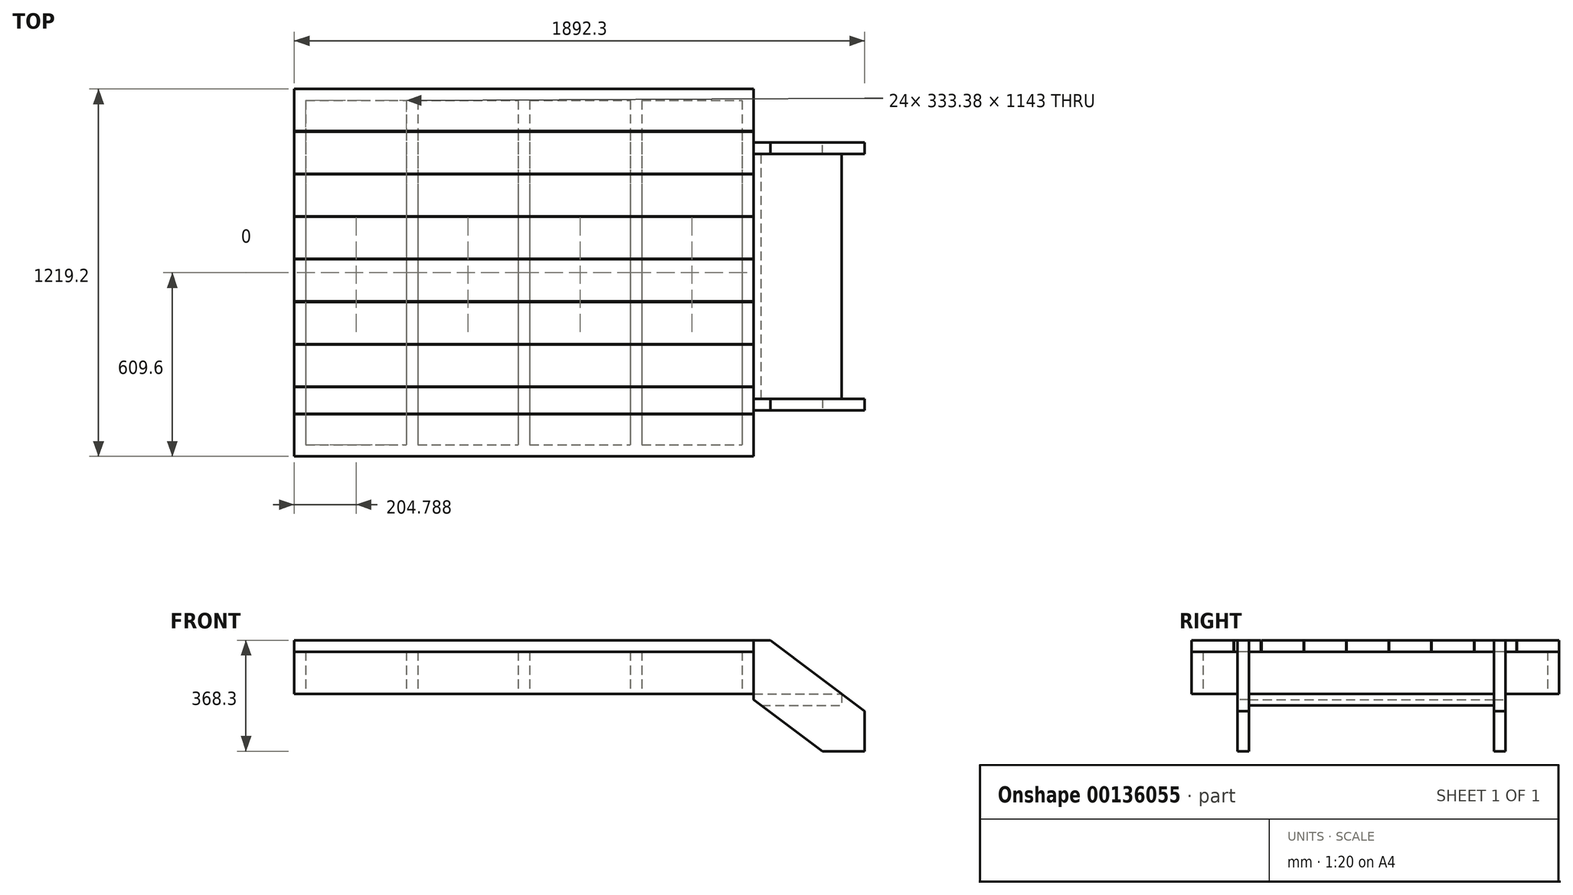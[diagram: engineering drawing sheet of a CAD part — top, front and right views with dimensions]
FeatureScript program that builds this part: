
annotation { "Feature Type Name" : "Feature", "Feature Type Description" : "" }
export const myFeature = defineFeature(function(context is Context, id is Id, definition is map)
    precondition{}
    {
        {
            var Q0;
            Q0=qCreatedBy(makeId("Top.planeOp"),FACE);
            var sketch = newSketch(context, id + "F0", { "sketchPlane" : qUnion([Q0])});
            skLineSegment(sketch, "E0.bottom", {"start": v(-762, 609.6) * mm, "end": v(762, 609.6) * mm});
            skLineSegment(sketch, "E0.top", {"start": v(-762, -609.6) * mm, "end": v(762, -609.6) * mm});
            skLineSegment(sketch, "E0.left", {"start": v(-762, 609.6) * mm, "end": v(-762, -609.6) * mm});
            skLineSegment(sketch, "E0.right", {"start": v(762, 609.6) * mm, "end": v(762, -609.6) * mm});
            skLineSegment(sketch, "E1.bottom", {"start": v(-723.9, 571.5) * mm, "end": v(-390.52, 571.5) * mm});
            skLineSegment(sketch, "E1.top", {"start": v(-723.9, -571.5) * mm, "end": v(-390.53, -571.5) * mm});
            skLineSegment(sketch, "E1.left", {"start": v(-723.9, 571.5) * mm, "end": v(-723.9, -571.5) * mm});
            skLineSegment(sketch, "E1.right", {"start": v(-390.52, 571.5) * mm, "end": v(-390.53, -571.5) * mm});
            skLineSegment(sketch, "E2.bottom", {"start": v(-352.42, 571.5) * mm, "end": v(-19.05, 571.5) * mm});
            skLineSegment(sketch, "E2.top", {"start": v(-352.43, -571.5) * mm, "end": v(-19.05, -571.5) * mm});
            skLineSegment(sketch, "E2.left", {"start": v(-352.42, 571.5) * mm, "end": v(-352.43, -571.5) * mm});
            skLineSegment(sketch, "E2.right", {"start": v(-19.05, 571.5) * mm, "end": v(-19.05, -571.5) * mm});
            skLineSegment(sketch, "E3.bottom", {"start": v(19.05, 571.5) * mm, "end": v(352.43, 571.5) * mm});
            skLineSegment(sketch, "E3.top", {"start": v(19.05, -571.5) * mm, "end": v(352.43, -571.5) * mm});
            skLineSegment(sketch, "E3.left", {"start": v(19.05, 571.5) * mm, "end": v(19.05, -571.5) * mm});
            skLineSegment(sketch, "E3.right", {"start": v(352.43, 571.5) * mm, "end": v(352.43, -571.5) * mm});
            skLineSegment(sketch, "E4", {"start": v(0, 0) * mm, "end": v(0, -270.05) * mm, "construction": true});
            skLineSegment(sketch, "E5", {"start": v(-150.6, 0) * mm, "end": v(0, 0) * mm, "construction": true});
            skLineSegment(sketch, "E6.bottom", {"start": v(390.53, 571.5) * mm, "end": v(723.9, 571.5) * mm});
            skLineSegment(sketch, "E6.top", {"start": v(390.52, -571.5) * mm, "end": v(723.9, -571.5) * mm});
            skLineSegment(sketch, "E6.left", {"start": v(390.53, 571.5) * mm, "end": v(390.52, -571.5) * mm});
            skLineSegment(sketch, "E6.right", {"start": v(723.9, 571.5) * mm, "end": v(723.9, -571.5) * mm});
            skSolve(sketch);
        }
        {
            var Q0;
            Q0=makeQuery(id+"F0.imprint","IMPRINT",FACE,{"disambiguationData":[TD([[makeQuery(id+"F0.imprint","IMPRINT",EDGE,{"derivedFrom":sQuery(id+"F0.wireOp",EDGE,"E0.bottom")}),-1.0]])]});
            extrude(context, id + "F1", {"entities" : qUnion([Q0]), "depth" : 139.7 * mm});
        }
        {
            var Q0;
            Q0=makeQuery(id+"F1.opExtrude","SWEPT_FACE",FACE,{"disambiguationData":[OSD([sQuery(id+"F0.wireOp",EDGE,"E0.left")])]});
            var sketch = newSketch(context, id + "F2", { "sketchPlane" : qUnion([Q0])});
            skLineSegment(sketch, "E7.bottom", {"start": v(-609.6, 177.8) * mm, "end": v(-469.9, 177.8) * mm});
            skLineSegment(sketch, "E7.top", {"start": v(-609.6, 139.7) * mm, "end": v(-469.9, 139.7) * mm});
            skLineSegment(sketch, "E7.left", {"start": v(-609.6, 177.8) * mm, "end": v(-609.6, 139.7) * mm});
            skLineSegment(sketch, "E7.right", {"start": v(-469.9, 177.8) * mm, "end": v(-469.9, 139.7) * mm});
            skLineSegment(sketch, "E8.bottom", {"start": v(-468.31, 177.8) * mm, "end": v(-328.61, 177.8) * mm});
            skLineSegment(sketch, "E8.top", {"start": v(-468.31, 139.7) * mm, "end": v(-328.61, 139.7) * mm});
            skLineSegment(sketch, "E8.left", {"start": v(-468.31, 177.8) * mm, "end": v(-468.31, 139.7) * mm});
            skLineSegment(sketch, "E8.right", {"start": v(-328.61, 177.8) * mm, "end": v(-328.61, 139.7) * mm});
            skLineSegment(sketch, "E9.bottom", {"start": v(-327.02, 177.8) * mm, "end": v(-187.32, 177.8) * mm});
            skLineSegment(sketch, "E9.top", {"start": v(-327.02, 139.7) * mm, "end": v(-187.32, 139.7) * mm});
            skLineSegment(sketch, "E9.left", {"start": v(-327.02, 177.8) * mm, "end": v(-327.02, 139.7) * mm});
            skLineSegment(sketch, "E9.right", {"start": v(-187.32, 177.8) * mm, "end": v(-187.32, 139.7) * mm});
            skLineSegment(sketch, "E10.bottom", {"start": v(-185.74, 177.8) * mm, "end": v(-46.04, 177.8) * mm});
            skLineSegment(sketch, "E10.top", {"start": v(-185.74, 139.7) * mm, "end": v(-46.04, 139.7) * mm});
            skLineSegment(sketch, "E10.left", {"start": v(-185.74, 177.8) * mm, "end": v(-185.74, 139.7) * mm});
            skLineSegment(sketch, "E10.right", {"start": v(-46.04, 177.8) * mm, "end": v(-46.04, 139.7) * mm});
            skLineSegment(sketch, "E11.bottom", {"start": v(-44.45, 177.8) * mm, "end": v(95.25, 177.8) * mm});
            skLineSegment(sketch, "E11.top", {"start": v(-44.45, 139.7) * mm, "end": v(95.25, 139.7) * mm});
            skLineSegment(sketch, "E11.left", {"start": v(-44.45, 177.8) * mm, "end": v(-44.45, 139.7) * mm});
            skLineSegment(sketch, "E11.right", {"start": v(95.25, 177.8) * mm, "end": v(95.25, 139.7) * mm});
            skLineSegment(sketch, "E12.bottom", {"start": v(96.84, 177.8) * mm, "end": v(236.54, 177.8) * mm});
            skLineSegment(sketch, "E12.top", {"start": v(96.84, 139.7) * mm, "end": v(236.54, 139.7) * mm});
            skLineSegment(sketch, "E12.left", {"start": v(96.84, 177.8) * mm, "end": v(96.84, 139.7) * mm});
            skLineSegment(sketch, "E12.right", {"start": v(236.54, 177.8) * mm, "end": v(236.54, 139.7) * mm});
            skLineSegment(sketch, "E13.bottom", {"start": v(238.13, 177.8) * mm, "end": v(377.83, 177.8) * mm});
            skLineSegment(sketch, "E13.top", {"start": v(238.13, 139.7) * mm, "end": v(377.83, 139.7) * mm});
            skLineSegment(sketch, "E13.left", {"start": v(238.13, 177.8) * mm, "end": v(238.13, 139.7) * mm});
            skLineSegment(sketch, "E13.right", {"start": v(377.83, 177.8) * mm, "end": v(377.83, 139.7) * mm});
            skLineSegment(sketch, "E14.bottom", {"start": v(379.41, 177.8) * mm, "end": v(468.31, 177.8) * mm});
            skLineSegment(sketch, "E14.top", {"start": v(379.41, 139.7) * mm, "end": v(468.31, 139.7) * mm});
            skLineSegment(sketch, "E14.left", {"start": v(379.41, 177.8) * mm, "end": v(379.41, 139.7) * mm});
            skLineSegment(sketch, "E14.right", {"start": v(468.31, 177.8) * mm, "end": v(468.31, 139.7) * mm});
            skLineSegment(sketch, "E15.bottom", {"start": v(469.9, 177.8) * mm, "end": v(609.6, 177.8) * mm});
            skLineSegment(sketch, "E15.top", {"start": v(469.9, 139.7) * mm, "end": v(609.6, 139.7) * mm});
            skLineSegment(sketch, "E15.left", {"start": v(469.9, 177.8) * mm, "end": v(469.9, 139.7) * mm});
            skLineSegment(sketch, "E15.right", {"start": v(609.6, 177.8) * mm, "end": v(609.6, 139.7) * mm});
            skSolve(sketch);
        }
        {
            var Q0;
            Q0=makeQuery(id+"F2.imprint","IMPRINT",FACE,{"disambiguationData":[TD([[makeQuery(id+"F2.imprint","IMPRINT",EDGE,{"derivedFrom":sQuery(id+"F2.wireOp",EDGE,"E10.bottom")}),-1.0]])]});
            var Q1;
            Q1=makeQuery(id+"F2.imprint","IMPRINT",FACE,{"disambiguationData":[TD([[makeQuery(id+"F2.imprint","IMPRINT",EDGE,{"derivedFrom":sQuery(id+"F2.wireOp",EDGE,"E11.bottom")}),-1.0]])]});
            var Q2;
            Q2=makeQuery(id+"F2.imprint","IMPRINT",FACE,{"disambiguationData":[TD([[makeQuery(id+"F2.imprint","IMPRINT",EDGE,{"derivedFrom":sQuery(id+"F2.wireOp",EDGE,"E14.bottom")}),-1.0]])]});
            var Q3;
            Q3=makeQuery(id+"F2.imprint","IMPRINT",FACE,{"disambiguationData":[TD([[makeQuery(id+"F2.imprint","IMPRINT",EDGE,{"derivedFrom":sQuery(id+"F2.wireOp",EDGE,"E15.bottom")}),-1.0]])]});
            var Q4;
            Q4=makeQuery(id+"F2.imprint","IMPRINT",FACE,{"disambiguationData":[TD([[makeQuery(id+"F2.imprint","IMPRINT",EDGE,{"derivedFrom":sQuery(id+"F2.wireOp",EDGE,"E12.bottom")}),-1.0]])]});
            var Q5;
            Q5=makeQuery(id+"F2.imprint","IMPRINT",FACE,{"disambiguationData":[TD([[makeQuery(id+"F2.imprint","IMPRINT",EDGE,{"derivedFrom":sQuery(id+"F2.wireOp",EDGE,"E13.bottom")}),-1.0]])]});
            var Q6;
            Q6=makeQuery(id+"F2.imprint","IMPRINT",FACE,{"disambiguationData":[TD([[makeQuery(id+"F2.imprint","IMPRINT",EDGE,{"derivedFrom":sQuery(id+"F2.wireOp",EDGE,"E7.bottom")}),-1.0]])]});
            var Q7;
            Q7=makeQuery(id+"F2.imprint","IMPRINT",FACE,{"disambiguationData":[TD([[makeQuery(id+"F2.imprint","IMPRINT",EDGE,{"derivedFrom":sQuery(id+"F2.wireOp",EDGE,"E8.bottom")}),-1.0]])]});
            var Q8;
            Q8=makeQuery(id+"F2.imprint","IMPRINT",FACE,{"disambiguationData":[TD([[makeQuery(id+"F2.imprint","IMPRINT",EDGE,{"derivedFrom":sQuery(id+"F2.wireOp",EDGE,"E9.bottom")}),-1.0]])]});
            var Q9;
            Q9=makeQuery(id+"F1.opExtrude","SWEPT_FACE",FACE,{"disambiguationData":[OSD([sQuery(id+"F0.wireOp",EDGE,"E0.right")])]});
            extrude(context, id + "F3", {"entities" : qUnion([Q0, Q1, Q2, Q3, Q4, Q5, Q6, Q7, Q8]), "endBound" : BoundingType.UP_TO_SURFACE, "oppositeDirection" : true, "endBoundEntityFace" : qUnion([Q9]), "depth" : 1524 * mm});
        }
        {
            var Q0;
            Q0=makeQuery(id+"F1.opExtrude","SWEPT_FACE",FACE,{"disambiguationData":[OSD([sQuery(id+"F0.wireOp",EDGE,"E0.top")])]});
            cPlane(context, id + "F4", {"entities" : qUnion([Q0]), "cplaneType" : CPlaneType.OFFSET, "offset" : 152.4 * mm, "oppositeDirection" : true, "width" : 152.4 * mm, "height" : 152.4 * mm});
        }
        {
            var Q0;
            Q0=qCreatedBy(id+"F4.planeOp",FACE);
            var sketch = newSketch(context, id + "F5", { "sketchPlane" : qUnion([Q0])});
            skLineSegment(sketch, "E16", {"start": v(762, 177.8) * mm, "end": v(762, -19.05) * mm});
            skLineSegment(sketch, "E17", {"start": v(762, -19.05) * mm, "end": v(990.6, -190.5) * mm});
            skLineSegment(sketch, "E18", {"start": v(990.6, -190.5) * mm, "end": v(1130.3, -190.5) * mm});
            skLineSegment(sketch, "E19", {"start": v(1130.3, -190.5) * mm, "end": v(1130.3, -57.15) * mm});
            skLineSegment(sketch, "E20", {"start": v(1130.3, -57.15) * mm, "end": v(817.03, 177.8) * mm});
            skLineSegment(sketch, "E21", {"start": v(817.03, 177.8) * mm, "end": v(762, 177.8) * mm});
            skLineSegment(sketch, "E22", {"start": v(762, 0) * mm, "end": v(1054.1, 0) * mm, "construction": true});
            skSolve(sketch);
        }
        {
            var Q0;
            Q0=makeQuery(id+"F5.imprint","IMPRINT",FACE,{"disambiguationData":[TD([[makeQuery(id+"F5.imprint","IMPRINT",EDGE,{"derivedFrom":sQuery(id+"F5.wireOp",EDGE,"E16")}),1.0]])]});
            extrude(context, id + "F6", {"entities" : qUnion([Q0]), "oppositeDirection" : true, "depth" : 38.1 * mm});
        }
        {
            var Q0;
            Q0=makeQuery(id+"F6.opExtrude","CAP_FACE",FACE,{"disambiguationData":[OSD([sQuery(id+"F5.wireOp",EDGE,"E16"),sQuery(id+"F5.wireOp",EDGE,"E17"),sQuery(id+"F5.wireOp",EDGE,"E18"),sQuery(id+"F5.wireOp",EDGE,"E19"),sQuery(id+"F5.wireOp",EDGE,"E20"),sQuery(id+"F5.wireOp",EDGE,"E21")])],"isStart":false});
            cPlane(context, id + "F7", {"entities" : qUnion([Q0]), "cplaneType" : CPlaneType.OFFSET, "offset" : 406.4 * mm, "width" : 152.4 * mm, "height" : 152.4 * mm});
        }
        {
            var Q0;
            Q0=makeQuery(id+"F6.opExtrude","SWEPT_BODY",BODY,{"disambiguationData":[OSD([sQuery(id+"F5.wireOp",EDGE,"E16"),sQuery(id+"F5.wireOp",EDGE,"E17"),sQuery(id+"F5.wireOp",EDGE,"E18"),sQuery(id+"F5.wireOp",EDGE,"E19"),sQuery(id+"F5.wireOp",EDGE,"E20"),sQuery(id+"F5.wireOp",EDGE,"E21")])]});
            var Q1;
            Q1=qCreatedBy(id+"F7.planeOp",FACE);
            mirror(context, id + "F8", {"entities" : qUnion([Q0]), "mirrorPlane" : qUnion([Q1])});
        }
        {
            var Q0;
            Q0=makeQuery(id+"F8.opPattern","COPY",FACE,{"derivedFrom":makeQuery(id+"F6.opExtrude","CAP_FACE",FACE,{"disambiguationData":[OSD([sQuery(id+"F5.wireOp",EDGE,"E16"),sQuery(id+"F5.wireOp",EDGE,"E17"),sQuery(id+"F5.wireOp",EDGE,"E18"),sQuery(id+"F5.wireOp",EDGE,"E19"),sQuery(id+"F5.wireOp",EDGE,"E20"),sQuery(id+"F5.wireOp",EDGE,"E21")])],"isStart":false}),"instanceName":"1"});
            var sketch = newSketch(context, id + "F9", { "sketchPlane" : qUnion([Q0])});
            skLineSegment(sketch, "E23.bottom", {"start": v(762, 0) * mm, "end": v(1054.1, 0) * mm});
            skLineSegment(sketch, "E23.top", {"start": v(762, -38.1) * mm, "end": v(1054.1, -38.1) * mm});
            skLineSegment(sketch, "E23.left", {"start": v(762, 0) * mm, "end": v(762, -38.1) * mm});
            skLineSegment(sketch, "E23.right", {"start": v(1054.1, 0) * mm, "end": v(1054.1, -38.1) * mm});
            skSolve(sketch);
        }
        {
            var Q0;
            {var subQ4=sQuery(id+"F9.wireOp",EDGE,"E23.bottom");Q0=makeQuery(id+"F9.imprint","IMPRINT",FACE,{"disambiguationData":[TD([[makeQuery(id+"F9.imprint","IMPRINT",EDGE,{"derivedFrom":subQ4}),-1.0]])]});}
            extrude(context, id + "F10", {"entities" : qUnion([Q0]), "endBound" : BoundingType.UP_TO_NEXT, "depth" : 25.4 * mm});
        }
    });
